# Revit family: Faucet-Single_Control-American_Standard-Colony_Pro-707505X_Series
name_source: partatom
category: Plumbing Fixtures
units: mm (PartAtom-declared; Revit-internal decimal feet)

## family parameters
Always vertical = No
Cut with Voids When Loaded = No
OmniClass Number = 23.45.55.14
OmniClass Title = Single Faucets
Part Type = Normal
Room Calculation Point = No
Round Connector Dimension = Use Diameter
Shared = Yes
Work Plane-Based = Yes

## types (4) — shared parameters
ADA Compliant = Yes
Assembly Code = D2020300
CEC Compliant = Yes
CW Connection = No
CWFU = 1.5
CalGreen Compliant = Yes
Compliance Certifications = These products meet or exceed the following codes and standards: ANSI A117.1, ASME A112.18.1,CSA B125.1,NSF 61/Section 9,NSF 372
Default Elevation = 0"
Drain Depth = 3"
Drain Width = 3"
Finish = Metal-American Standard-002-Polished Chrome
Flow Rate = 0.5 gpm(1.9 L/min)
HW Connection = No
HWFU = 1.5
Height = 5 15/16"
Installation Type = Deck Mounted
Length = 6 3/8"
Manufacturer = American Standard
Material = Metal-American Standard-002-Polished Chrome
Product Documentation Link = https://americanstandard.box.com
Product Page URL = https://www.americanstandard-us.com
Revised Date = 09/23/2022
Tempered Water Connection = Yes
Tempered Water Connection Diameter = 3/8"
URL = http://www.americanstandard-us.com
Vent Connection = No
WFU = 2
Waste Connection = No
Width = 6"

## per-type parameters (varying)
| type | Description | Drain Visibility | Grid Drain | Pop Up Drain |
| 7075050.002 | Colony® PRO 4-Inch Centerset Single-Handle Bathroom Faucet 0.5 gpm/1.9 L/min With Lever Handle | Yes | No | Yes |
| 7075054.002 | Colony® PRO 4-Inch Centerset Single-Handle Bathroom Faucet 0.5 gpm/1.9 L/min Less Drain With Lever Handle | No | No | No |
| 7075055.002 | Colony® PRO 4-Inch Centerset Single-Handle Bathroom Faucet 0.5 gpm/1.9 L/min Less Drain With Lever Handle | No | No | No |
| 7075056.002 | Colony® PRO 4-Inch Centerset Single-Handle Bathroom Faucet 0.5 gpm/1.9 L/min With Lever Handle | Yes | Yes | No |

note: column(s) folded — value = type name in every type: Model

## geometry (parser evidence)
native form markers: Sweep x5
no freeform markers — native parametric forms only
